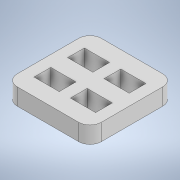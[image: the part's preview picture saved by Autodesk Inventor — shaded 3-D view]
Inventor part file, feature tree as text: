
AUTODESK INVENTOR PART (.ipt)
format: ipt  version: 2020 (Build 240168000, 168)  size: 124,416 bytes
history: native  units: in
note: dims shown in document units (in); Inventor stores cm internally (conversion verified against a paired STEP export)
features: extrude x1, sketch x1
ambient origin geometry x8: Origin, YZ Plane, XZ Plane, XY Plane, X Axis, Y Axis, Z Axis, Center Point
bodies: Solid1 (feature_tree)
feature tree (2):
  extrude  "Extrusion1"  Depth=0.4331in
  sketch  "Sketch1"  dims[d0=0.0787in d1=0.4331in d2=0.4331in d5=0.1181in d6=0.1772in d7=0.0787in d8=0.1181in d11=0.1181in d12=0.0in]
